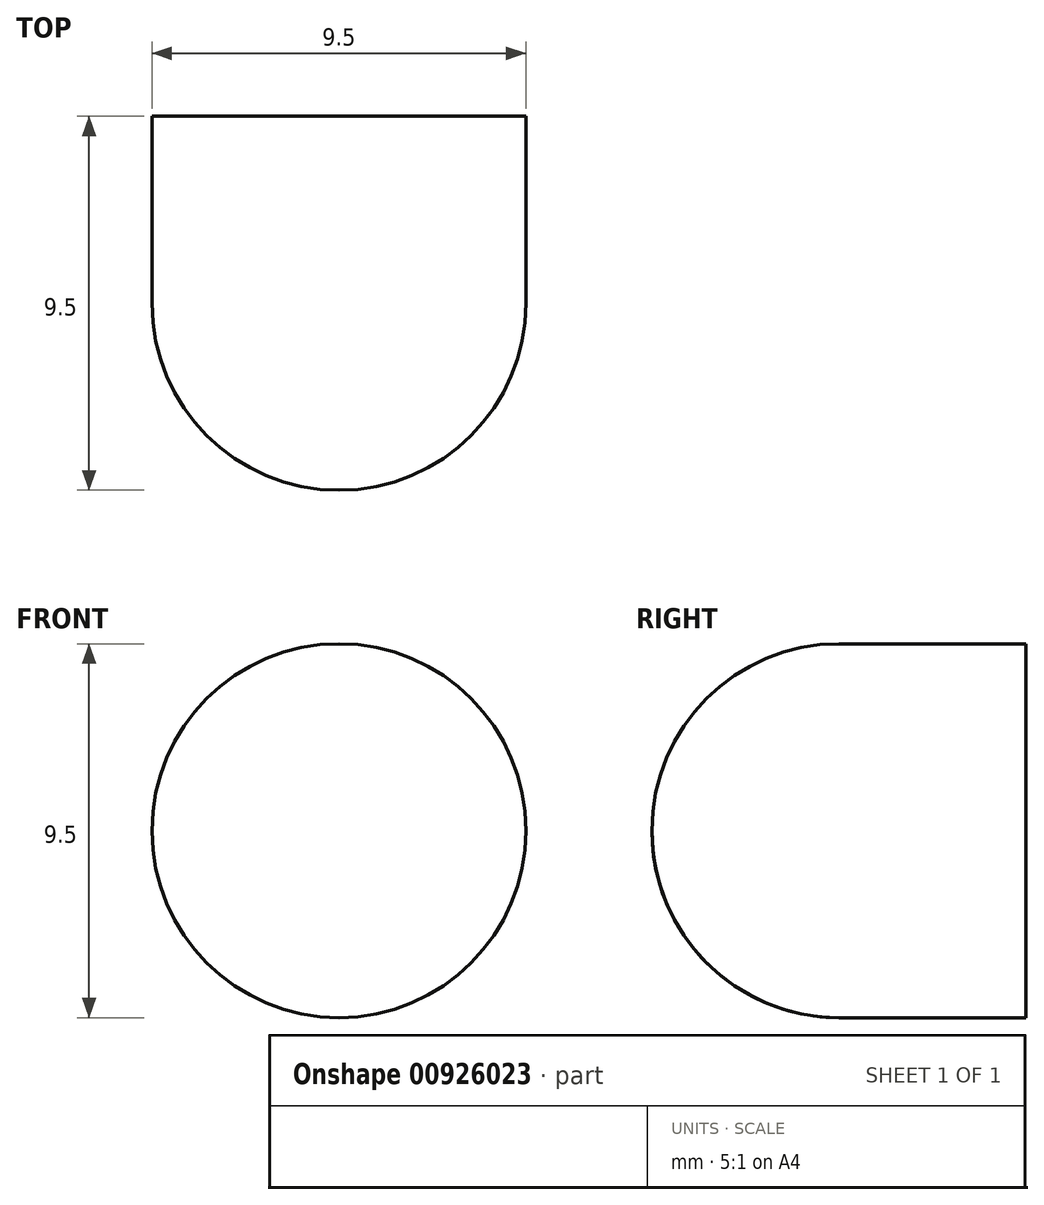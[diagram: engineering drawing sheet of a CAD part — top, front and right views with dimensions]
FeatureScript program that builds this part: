
annotation { "Feature Type Name" : "Feature", "Feature Type Description" : "" }
export const myFeature = defineFeature(function(context is Context, id is Id, definition is map)
    precondition{}
    {
        {
            var Q0;
            Q0=qCreatedBy(makeId("Front.planeOp"),FACE);
            var sketch = newSketch(context, id + "F0", { "sketchPlane" : qUnion([Q0])});
            skCircle(sketch, "E0", {"center": v(0, 0) * mm, "radius": 4.75 * mm});
            skSolve(sketch);
        }
        {
            var Q0;
            Q0=makeQuery(id+"F0.imprint","IMPRINT",FACE,{"disambiguationData":[TD([[makeQuery(id+"F0.imprint","IMPRINT",EDGE,{"derivedFrom":sQuery(id+"F0.wireOp",EDGE,"E0")}),1.0]])]});
            extrude(context, id + "F1", {"entities" : qUnion([Q0]), "endBound" : BoundingType.SYMMETRIC, "depth" : 9.5 * mm, "offsetDistance" : 25 * mm});
        }
        {
            var Q0;
            Q0=makeQuery(id+"F1.opExtrude","CAP_EDGE",EDGE,{"disambiguationData":[OSD([sQuery(id+"F0.wireOp",EDGE,"E0")])],"isStart":false});
            fillet(context, id + "F2", {"entities" : qUnion([Q0]), "radius" : 4.75 * mm, "tangentPropagation" : true, "allowEdgeOverflow" : false});
        }
    });
